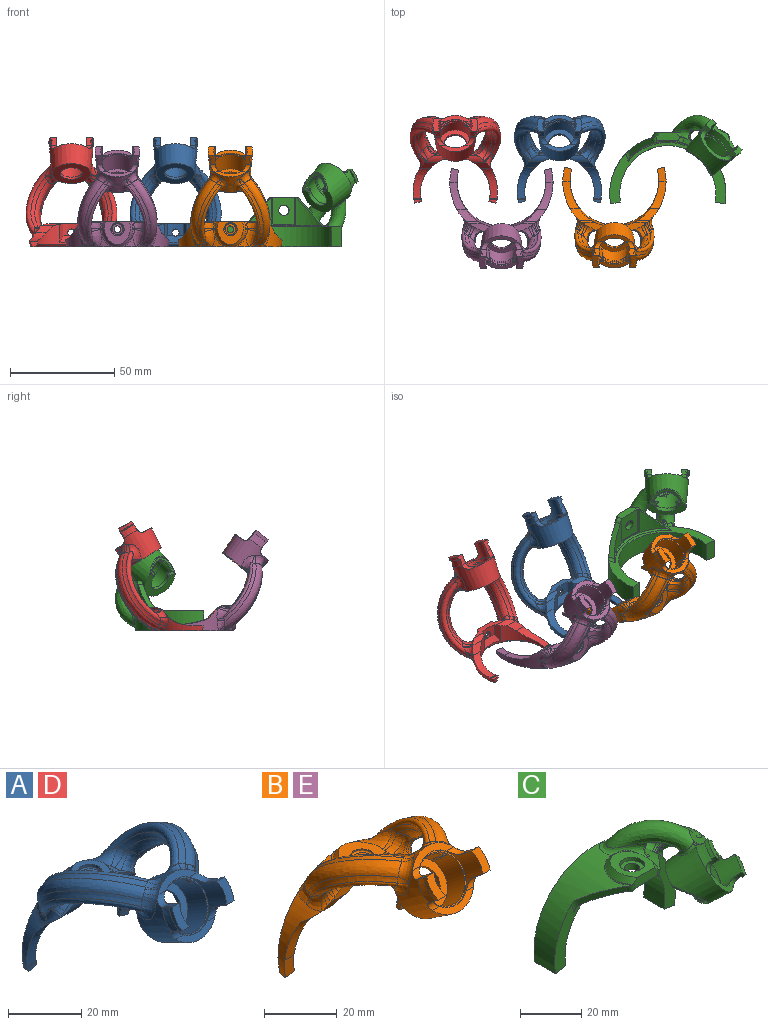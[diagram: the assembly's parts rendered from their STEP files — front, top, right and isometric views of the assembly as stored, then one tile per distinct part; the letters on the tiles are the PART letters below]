
ASSEMBLY  parts=5 mates=4
PART A: 145 faces, bbox 61.8x56.7x51.6 mm
  f0: cylinder r=1.71mm len=3.43mm, axis (0,0,-1), area 13.7mm2, adj f45,f46,f143
  f1: revolved ~9.98x7.31mm, area 15mm2, adj f23,f85,f86,f87,f132,f135
  f2: revolved ~9.98x7.51mm, area 16mm2, adj f23,f90,f92,f94,f130,f136
  f3: cone r=10.34mm half-angle=5deg, axis (0,-0.86,0.52), area 401.5mm2, adj f6,f7,f28,f50,f56,f57,f58,f59
  f4: revolved ~19.01x6.39mm, area 63.4mm2, adj f20,f23,f39,f40,f74,f75,f77
  f5: cone r=10.34mm half-angle=5deg, axis (0,-0.86,0.52), area 51.2mm2, adj f28,f53,f106,f108,f110,f116,f118,f120
  f6: cone r=10.34mm half-angle=8.4deg, axis (0,0.86,-0.52), area 23.4mm2, adj f3,f15,f51,f54,f58,f59
  f7: cone r=10.34mm half-angle=8.4deg, axis (0,0.86,-0.52), area 23.4mm2, adj f3,f16,f52,f55,f56,f57
  f8: plane 6.17x3.73mm, normal (0,0.86,-0.52), area 2.5mm2, adj f15,f18,f51,f54
  f9: plane 6.17x3.73mm, normal (0,0.86,-0.52), area 2.5mm2, adj f16,f17,f52,f55
  f10: cylinder r=10.72mm len=6.86mm, axis (0,0.86,-0.52), area 9.8mm2, adj f12,f18,f51,f54
  f11: cylinder r=10.72mm len=6.86mm, axis (0,0.86,-0.52), area 9.8mm2, adj f13,f17,f52,f55
  f12: plane 6.17x3.73mm, normal (0,-0.86,0.52), area 19.8mm2, adj f10,f14,f51,f54
  f13: plane 6.17x3.73mm, normal (0,-0.86,0.52), area 19.8mm2, adj f11,f14,f52,f55
  f14: cylinder r=8.05mm len=18.05mm, axis (0,0.86,-0.52), area 155.6mm2, adj f12,f13,f29,f50,f51,f52,f53,f54
  f15: cone r=9.87mm half-angle=40.8deg, axis (0,-0.86,0.52), area 2.8mm2, adj f6,f8,f51,f54
  f16: cone r=9.87mm half-angle=40.8deg, axis (0,-0.86,0.52), area 2.8mm2, adj f7,f9,f52,f55
  f17: cone r=10.46mm half-angle=45deg, axis (0,-0.86,0.52), area 2.6mm2, adj f9,f11,f52,f55
  f18: cone r=10.46mm half-angle=45deg, axis (0,-0.86,0.52), area 2.6mm2, adj f8,f10,f51,f54
  f19: plane 3.35x2.31mm, normal (-0.26,0,-0.97), area 6.5mm2, adj f21,f22,f23,f44,f49
  f20: plane 3.35x2.31mm, normal (0.26,0,-0.97), area 6.5mm2, adj f4,f21,f23,f39,f49
  f21: cylinder r=16.68mm len=33.35mm, axis (0,-1,0), area 210.6mm2, adj f19,f20,f39,f40,f41,f42,f43,f44
  f22: revolved ~18.79x6.34mm, area 62.2mm2, adj f19,f23,f42,f44,f93,f95,f97
  f23: plane 39.71x25.22mm, normal (0,1,0), area 110.1mm2, adj f1,f2,f4,f19,f20,f22,f49,f79
  f24: bspline ~37.35x28.39mm, area 142.5mm2, adj f72,f73,f74,f76,f78,f80,f123,f125
  f25: bspline ~37.42x27.73mm, area 153.3mm2, adj f70,f71,f83,f85,f120,f122
  f26: bspline ~41.55x31.99mm, area 181.1mm2, adj f71,f72,f77,f79,f115,f116,f117,f119
  f27: bspline ~33.51x27.06mm, area 100.4mm2, adj f70,f73,f84,f86,f126
  f28: plane 18.73x16.07mm, normal (0,0.86,-0.52), area 177.7mm2, adj f3,f5,f32,f109,f111,f112,f113,f114
  f29: plane 16.1x13.78mm, normal (0,-0.86,0.52), area 18.8mm2, adj f14,f30
  f30: cylinder r=7.67mm len=17.65mm, axis (0,0.86,-0.52), area 409.3mm2, adj f29,f31,f33,f60,f61,f62,f63,f64
  f31: plane 15.34x13.13mm, normal (0,-0.86,0.52), area 97mm2, adj f30,f32
  f32: cylinder r=5.29mm len=10.58mm, axis (0,0.86,-0.52), area 39.6mm2, adj f28,f31
  f33: bspline ~2.64x2.2mm, area 0.4mm2, adj f30,f34,f62,f64
  f34: plane 2.43x2.08mm, normal (0.71,-0.33,-0.62), area 1.2mm2, adj f33,f64
  f35: bspline ~37.68x29.01mm, area 144.5mm2, adj f68,f69,f97,f99,f100,f101,f107,f109
  f36: bspline ~41.92x32.7mm, area 183.6mm2, adj f67,f68,f91,f93,f102,f103,f104,f106
  f37: bspline ~37.76x28.35mm, area 155.8mm2, adj f66,f67,f88,f90,f110,f112
  f38: bspline ~33.81x27.63mm, area 102.1mm2, adj f66,f69,f94,f96,f113
  f39: plane 3.8x2.15mm, normal (0,-1,-0.01), area 6mm2, adj f4,f20,f21,f40
  f40: extruded ~15.06x8.21mm, area 65.8mm2, adj f4,f21,f39,f41,f76
  f41: plane 9.07x3.65mm, normal (0,-0.65,-0.76), area 23.4mm2, adj f21,f40,f78,f141
  f42: extruded ~15.06x8.21mm, area 65.7mm2, adj f21,f22,f43,f44,f99
  f43: plane 9.02x3.6mm, normal (0,-0.65,-0.76), area 23.4mm2, adj f21,f42,f101,f140
  f44: plane 3.8x2.15mm, normal (0,-1,-0.01), area 6mm2, adj f19,f21,f22,f42
  f45: cylinder r=18.71mm len=8.04mm, axis (0,1,0), area 37.7mm2, adj f0,f46,f47,f48,f139
  f46: cone r=18.71mm half-angle=34.2deg, axis (0,-1,0), area 35mm2, adj f0,f21,f45,f47,f48
  f47: plane 8.92x2.67mm, normal (-0.87,0,-0.5), area 20.9mm2, adj f21,f45,f46,f139,f140
  f48: plane 8.92x2.67mm, normal (0.87,0,-0.5), area 20.9mm2, adj f21,f45,f46,f139,f141
  f49: cone r=17.95mm half-angle=45deg, axis (0,1,0), area 114mm2, adj f19,f20,f21,f23
  f50: plane 15.23x2.96mm, normal (0,-0.86,0.52), area 27.9mm2, adj f3,f14,f57,f58
  f51: plane 3.92x2.9mm, normal (0,-0.52,-0.86), area 11.1mm2, adj f6,f8,f10,f12,f14,f15,f18,f58
  f52: plane 3.92x2.9mm, normal (0,-0.52,-0.86), area 11.1mm2, adj f7,f9,f11,f13,f14,f16,f17,f57
  f53: plane 15.28x3.01mm, normal (0,-0.86,0.52), area 27.9mm2, adj f5,f14,f56,f59,f104,f115
  f54: plane 3.92x2.9mm, normal (0,0.52,0.86), area 11.1mm2, adj f6,f8,f10,f12,f14,f15,f18,f59
  f55: plane 3.92x2.9mm, normal (0,0.52,0.86), area 11.1mm2, adj f7,f9,f11,f13,f14,f16,f17,f56
  f56: cylinder r=3.05mm len=5.14mm, axis (1,0,0), area 11.9mm2, adj f3,f7,f14,f53,f55,f117
  f57: cylinder r=3.05mm len=5.14mm, axis (-1,0,0), area 12.3mm2, adj f3,f7,f14,f50,f52
  f58: cylinder r=3.05mm len=5.14mm, axis (-1,0,0), area 12.3mm2, adj f3,f6,f14,f50,f51
  f59: cylinder r=3.05mm len=5.14mm, axis (1,0,0), area 11.9mm2, adj f3,f6,f14,f53,f54,f102
  f60: plane 0.56x0.38mm, normal (0.5,-0.45,-0.74), area 0.2mm2, adj f30,f62
  f61: plane 0.59x0.48mm, normal (1,0,0), area 0.2mm2, adj f30,f62
  f62: torus R=7.67mm, axis (0,0.86,-0.52), area 14.1mm2, adj f30,f33,f60,f61
  f63: plane 3.47x3.23mm, normal (0,0.86,-0.52), area 0.7mm2, adj f30,f65
  f64: plane 2.52x2.17mm, normal (0,0.86,-0.52), area 1.3mm2, adj f30,f33,f34
  f65: bspline ~3.11x2.87mm, area 0mm2, adj f30,f63
  f66: bspline ~26.78x13.96mm, area 61.4mm2, adj f37,f38,f92,f114
  f67: bspline ~36.44x19.97mm, area 96.7mm2, adj f36,f37,f89,f108
  f68: bspline ~35.96x20.27mm, area 92.1mm2, adj f35,f36,f95,f105
  f69: bspline ~25.43x11.92mm, area 58.4mm2, adj f35,f38,f98,f111
  f70: bspline ~26.88x14.18mm, area 60.2mm2, adj f25,f27,f87,f124
  f71: bspline ~36.63x19.85mm, area 95.2mm2, adj f25,f26,f81,f118
  f72: bspline ~36.32x20.23mm, area 91mm2, adj f24,f26,f75,f121
  f73: bspline ~26.06x11.92mm, area 57.5mm2, adj f24,f27,f82,f127
  f74: bspline ~4.95x4.54mm, area 10.4mm2, adj f4,f24,f75,f76
  f75: bspline ~4.6x3.59mm, area 5.8mm2, adj f4,f72,f74,f77
  f76: bspline ~4.82x1.66mm, area 1.4mm2, adj f24,f40,f74,f78
  f77: bspline ~4.12x4.07mm, area 7mm2, adj f4,f26,f75,f79
  f78: bspline ~7.43x4.67mm, area 15.9mm2, adj f24,f41,f76,f80
  f79: bspline ~4.9x4.45mm, area 8.3mm2, adj f23,f26,f77,f81
  f80: bspline ~5.35x4.42mm, area 4mm2, adj f24,f78,f82,f135
  f81: bspline ~2.23x2.21mm, area 3.1mm2, adj f23,f71,f79,f83
  f82: bspline ~5.38x4.83mm, area 8.9mm2, adj f73,f80,f84,f135
  f83: bspline ~4.27x3.14mm, area 5.5mm2, adj f23,f25,f81,f85
  f84: bspline ~7.41x6.36mm, area 19.1mm2, adj f27,f82,f86,f135
  f85: bspline ~8.52x5.93mm, area 28.3mm2, adj f1,f25,f83,f87
  f86: bspline ~5.81x5.01mm, area 8.1mm2, adj f1,f27,f84,f87
  f87: bspline ~5.9x5.71mm, area 11.1mm2, adj f1,f70,f85,f86
  f88: bspline ~4.19x3.05mm, area 5.3mm2, adj f23,f37,f89,f90
  f89: bspline ~2.45x2.27mm, area 2.6mm2, adj f23,f67,f88,f91
  f90: bspline ~8.51x6.25mm, area 27.7mm2, adj f2,f37,f88,f92
  f91: bspline ~4.59x4.34mm, area 7.9mm2, adj f23,f36,f89,f93
  f92: bspline ~5.96x5.71mm, area 11mm2, adj f2,f66,f90,f94
  f93: bspline ~4.04x3.98mm, area 6.2mm2, adj f22,f36,f91,f95
  f94: bspline ~5.8x4.97mm, area 9.3mm2, adj f2,f38,f92,f96
  f95: bspline ~4.79x4.1mm, area 5.8mm2, adj f22,f68,f93,f97
  f96: bspline ~7.04x6.2mm, area 18.8mm2, adj f38,f94,f98,f136
  f97: bspline ~4.94x4.53mm, area 10.9mm2, adj f22,f35,f95,f99
  f98: bspline ~5.01x4.29mm, area 9.3mm2, adj f69,f96,f100,f136
  f99: bspline ~5.07x1.75mm, area 1.7mm2, adj f35,f42,f97,f101
  f100: bspline ~5.51x4.35mm, area 3.8mm2, adj f35,f98,f101,f136
  f101: bspline ~7.24x4.5mm, area 16.3mm2, adj f35,f43,f99,f100
  f102: bspline ~4.68x2.61mm, area 4.9mm2, adj f36,f59,f103,f104
  f103: bspline ~4.3x2.78mm, area 4.5mm2, adj f3,f36,f102,f105
  f104: bspline ~4.31x3.58mm, area 7.9mm2, adj f36,f53,f102,f106
  f105: bspline ~4.28x3.35mm, area 6.7mm2, adj f3,f68,f103,f107
  f106: bspline ~4.48x4.06mm, area 2.6mm2, adj f5,f36,f104,f108
  f107: bspline ~8.07x7.07mm, area 32.8mm2, adj f3,f35,f105,f109
  f108: bspline ~5.63x4.91mm, area 6.6mm2, adj f5,f67,f106,f110
  f109: bspline ~4.59x3.99mm, area 3mm2, adj f28,f35,f107,f111
  f110: bspline ~8.42x5.7mm, area 32.1mm2, adj f5,f37,f108,f112
  f111: bspline ~4.41x4.21mm, area 7.9mm2, adj f28,f69,f109,f113
  f112: bspline ~4.59x4.07mm, area 3.3mm2, adj f28,f37,f110,f114
  f113: bspline ~6.86x6.15mm, area 19.8mm2, adj f28,f38,f111,f114
  f114: bspline ~4.88x4.18mm, area 7.7mm2, adj f28,f66,f112,f113
  f115: bspline ~4.3x3.41mm, area 7.4mm2, adj f26,f53,f116,f117
  f116: bspline ~4.74x4.27mm, area 3.2mm2, adj f5,f26,f115,f118
  f117: bspline ~4.79x2.54mm, area 4.6mm2, adj f26,f56,f115,f119
  f118: bspline ~5.48x4.68mm, area 6.5mm2, adj f5,f71,f116,f120
  f119: bspline ~4.37x3.28mm, area 4.9mm2, adj f3,f26,f117,f121
  f120: bspline ~8.77x5.83mm, area 31.6mm2, adj f5,f25,f118,f122
  f121: bspline ~4.23x3.71mm, area 6.6mm2, adj f3,f72,f119,f123
  f122: bspline ~4.69x4.02mm, area 3.6mm2, adj f25,f28,f120,f124
  f123: bspline ~8.17x7.09mm, area 32.4mm2, adj f3,f24,f121,f125
  f124: bspline ~4.87x4.1mm, area 7.6mm2, adj f28,f70,f122,f126
  f125: bspline ~4.58x3.99mm, area 3.3mm2, adj f24,f28,f123,f127
  f126: bspline ~6.85x6.08mm, area 19.6mm2, adj f27,f28,f124,f127
  f127: bspline ~4.34x4.21mm, area 7.8mm2, adj f28,f73,f125,f126
  f128: plane 10.44x9.55mm, normal (0,0,1), area 49mm2, adj f129,f133,f138,f139,f142
  f129: bspline ~12.16x10.1mm, area 37.9mm2, adj f128,f130,f131,f132,f133,f138
  f130: bspline ~10.56x6.01mm, area 9.4mm2, adj f2,f129,f131,f137
  f131: bspline ~3.34x0.73mm, area 1.8mm2, adj f23,f129,f130,f132
  f132: bspline ~10.55x6.11mm, area 9.5mm2, adj f1,f129,f131,f134
  f133: extruded ~1.27x1.03mm, area 1.7mm2, adj f128,f129,f134,f139
  f134: extruded ~1.02x0.69mm, area 0.9mm2, adj f132,f133,f135,f139
  f135: cylinder r=20.42mm len=8.45mm, axis (0,1,0), area 7.6mm2, adj f1,f80,f82,f84,f134,f139,f141
  f136: cylinder r=20.42mm len=8.45mm, axis (0,1,0), area 7.6mm2, adj f2,f96,f98,f100,f137,f139,f140
  f137: extruded ~1.02x0.69mm, area 0.9mm2, adj f130,f136,f138,f139
  f138: extruded ~1.27x1.04mm, area 1.7mm2, adj f128,f129,f137,f139
  f139: plane 21.33x3.84mm, normal (0,-1,0), area 43.9mm2, adj f45,f47,f48,f128,f133,f134,f135,f136
  f140: cylinder r=5.08mm len=10mm, axis (-1,0,0), area 21.7mm2, adj f21,f43,f47,f136,f139
  f141: cylinder r=5.08mm len=10mm, axis (-1,0,0), area 21.7mm2, adj f21,f41,f48,f135,f139
  f142: cylinder r=3.17mm len=6.35mm, axis (0,0,1), area 17.7mm2, adj f128,f144
  f143: plane 5.59x5.59mm, normal (0,0,1), area 15.3mm2, adj f0,f144
  f144: torus R=2.79mm, axis (0,0,1), area 11.4mm2, adj f142,f143
PART B: 144 faces, bbox 51.7x52.7x52.5 mm
  f0: revolved ~5.9x5.45mm, area 16.2mm2, adj f1,f142,f143
  f1: bspline ~9.37x6.34mm, area 36.9mm2, adj f0,f2,f139,f140,f141
  f2: bspline ~3.52x1.42mm, area 2.6mm2, adj f1,f3,f138,f142
  f3: bspline ~1.16x0.78mm, area 0.5mm2, adj f2,f4,f138,f139
  f4: bspline ~2.44x0.93mm, area 1mm2, adj f3,f5,f137,f138
  f5: bspline ~4.62x2.02mm, area 1.5mm2, adj f4,f6,f136,f138
  f6: plane 31.53x6.21mm, normal (0,-1,0), area 81.9mm2, adj f5,f7,f115,f116,f117,f118,f119,f120
  f7: bspline ~7.06x6.66mm, area 17.5mm2, adj f6,f8,f115,f137
  f8: bspline ~31.43x23.43mm, area 79.9mm2, adj f7,f9,f113,f114,f115,f137
  f9: bspline ~7.85x6mm, area 21.3mm2, adj f8,f10,f111,f112
  f10: bspline ~4.41x4.15mm, area 5.6mm2, adj f9,f11,f111,f113
  f11: bspline ~4.68x3.98mm, area 3.4mm2, adj f10,f12,f110,f111
  f12: bspline ~7.34x7.29mm, area 24.7mm2, adj f11,f13,f77,f110
  f13: bspline ~3.66x3.46mm, area 4.1mm2, adj f12,f14,f76,f77
  f14: bspline ~29.57x16.47mm, area 58.5mm2, adj f13,f15,f75,f110
  f15: bspline ~37.48x26.76mm, area 197.7mm2, adj f14,f16,f18,f71,f76
  f16: bspline ~4.26x4mm, area 8.3mm2, adj f15,f17,f18,f143
  f17: bspline ~2.32x1.83mm, area 2.2mm2, adj f16,f71,f141,f143
  f18: bspline ~6.58x3.99mm, area 14.2mm2, adj f15,f16,f19,f75
  f19: revolved ~25.27x10.85mm, area 119.7mm2, adj f18,f20,f65,f66,f67,f70,f75,f143
  f20: plane 3.32x2.46mm, normal (-0.26,0,-0.97), area 7.2mm2, adj f19,f21,f61,f65,f143
  f21: cone r=22.48mm half-angle=45deg, axis (0,1,0), area 143.8mm2, adj f20,f22,f61,f143
  f22: plane 3.32x2.46mm, normal (0.26,0,-0.97), area 7.2mm2, adj f21,f23,f60,f61,f143
  f23: revolved ~25.27x10.85mm, area 119.7mm2, adj f22,f24,f25,f57,f58,f59,f60,f143
  f24: extruded ~13.06x7.87mm, area 47.1mm2, adj f23,f59,f60,f61,f127
  f25: bspline ~6.36x3.99mm, area 14.2mm2, adj f23,f26,f56,f57
  f26: bspline ~37.36x26.53mm, area 197.7mm2, adj f25,f27,f54,f55,f56
  f27: bspline ~30.31x17.11mm, area 63mm2, adj f26,f28,f52,f53
  f28: bspline ~32.11x22.21mm, area 73.8mm2, adj f27,f29,f30,f49,f50,f51
  f29: bspline ~3.34x2.6mm, area 5.3mm2, adj f28,f30,f52,f143
  f30: bspline ~9.45x6.34mm, area 36.9mm2, adj f28,f29,f31,f46,f48
  f31: bspline ~5.88x5.41mm, area 8.6mm2, adj f30,f32,f45,f49
  f32: bspline ~7.73x7.32mm, area 19.3mm2, adj f31,f33,f34,f132,f133
  f33: bspline ~2.1x0.93mm, area 1mm2, adj f32,f45,f134,f138
  f34: bspline ~31.34x23.25mm, area 79.9mm2, adj f32,f35,f44,f49,f131,f132
  f35: bspline ~7.65x5.73mm, area 21.3mm2, adj f34,f36,f37,f111
  f36: bspline ~4.62x3.32mm, area 5.4mm2, adj f35,f49,f50,f111
  f37: bspline ~4.07x3.8mm, area 5.6mm2, adj f35,f38,f44,f111
  f38: bspline ~4.68x3.98mm, area 3.4mm2, adj f37,f39,f41,f111
  f39: bspline ~7.28x7.11mm, area 24.7mm2, adj f38,f40,f41,f77
  f40: bspline ~3.67x3.46mm, area 4.1mm2, adj f39,f54,f55,f77
  f41: bspline ~31.99x22.24mm, area 63.3mm2, adj f38,f39,f42,f43,f44,f55,f58,f129
  f42: bspline ~6.43x3.18mm, area 5.9mm2, adj f41,f43,f128,f129
  f43: bspline ~6.48x2.48mm, area 7.3mm2, adj f41,f42,f58,f59
  f44: bspline ~18.17x8.9mm, area 29.3mm2, adj f34,f37,f41,f130
  f45: bspline ~1.29x0.79mm, area 0.5mm2, adj f31,f33,f46,f138
  f46: bspline ~3.42x1.38mm, area 2.6mm2, adj f30,f45,f47,f138
  f47: bspline ~8.27x7.02mm, area 6.9mm2, adj f46,f48,f138,f143
  f48: revolved ~5.9x5.43mm, area 16.2mm2, adj f30,f47,f143
  f49: bspline ~19.92x10.54mm, area 33.9mm2, adj f28,f31,f34,f36
  f50: bspline ~5.03x3.37mm, area 3.5mm2, adj f28,f36,f51,f111
  f51: bspline ~7.67x5.95mm, area 25.3mm2, adj f28,f50,f53,f77
  f52: bspline ~2.22x1.83mm, area 2.2mm2, adj f27,f29,f56,f143
  f53: bspline ~4.08x3.49mm, area 3.9mm2, adj f27,f51,f54,f77
  f54: bspline ~6.37x5.96mm, area 25.9mm2, adj f26,f40,f53,f77
  f55: bspline ~30.38x17.67mm, area 58.5mm2, adj f26,f40,f41,f57
  f56: bspline ~4.26x4mm, area 8.3mm2, adj f25,f26,f52,f143
  f57: bspline ~4x2.79mm, area 3.8mm2, adj f23,f25,f55,f58
  f58: bspline ~6.77x5.55mm, area 18.5mm2, adj f23,f41,f43,f57
  f59: extruded ~10.01x5.6mm, area 39.4mm2, adj f23,f24,f43,f127,f128
  f60: plane 6.61x4.24mm, normal (0,-1,-0.09), area 21.7mm2, adj f22,f23,f24,f61
  f61: cylinder r=21.21mm len=42.42mm, axis (0,-1,0), area 188.4mm2, adj f20,f21,f22,f24,f60,f62,f65,f66
  f62: cone r=21.21mm half-angle=49.7deg, axis (0,-1,0), area 33.6mm2, adj f61,f63,f64,f120,f121,f126
  f63: plane 5.59x0.59mm, normal (0.98,0,0.2), area 1.5mm2, adj f62,f121,f126
  f64: plane 5.59x0.59mm, normal (-0.98,0,0.2), area 1.5mm2, adj f62,f120,f121
  f65: plane 6.61x4.24mm, normal (0,-1,-0.09), area 21.7mm2, adj f19,f20,f61,f66
  f66: extruded ~13.06x7.87mm, area 47.1mm2, adj f19,f61,f65,f67,f119
  f67: extruded ~10.01x5.6mm, area 39.4mm2, adj f19,f66,f68,f118,f119
  f68: bspline ~6.42x2.52mm, area 7.3mm2, adj f67,f69,f70,f110
  f69: bspline ~5.63x2.66mm, area 5.9mm2, adj f68,f110,f117,f118
  f70: bspline ~7.41x5.93mm, area 18.5mm2, adj f19,f68,f75,f110
  f71: bspline ~30.59x17.18mm, area 63mm2, adj f15,f17,f72,f140
  f72: bspline ~4.14x3.53mm, area 3.9mm2, adj f71,f73,f76,f77
  f73: bspline ~7.3x5.58mm, area 25.3mm2, adj f72,f74,f77,f140
  f74: bspline ~5.03x3.37mm, area 3.5mm2, adj f73,f111,f112,f140
  f75: bspline ~4.01x2.74mm, area 3.8mm2, adj f14,f18,f19,f70
  f76: bspline ~6.37x5.96mm, area 25.9mm2, adj f13,f15,f72,f77
  f77: cone r=10.34mm half-angle=5deg, axis (0,-0.78,0.62), area 474.5mm2, adj f12,f13,f39,f40,f51,f53,f54,f72
  f78: cylinder r=2.54mm len=4.48mm, axis (-1,0,0), area 10.6mm2, adj f77,f79,f99,f109
  f79: cylinder r=8.05mm len=17.74mm, axis (0,0.78,-0.62), area 152.6mm2, adj f78,f80,f83,f86,f99,f101,f102,f103
  f80: plane 5.64x4.49mm, normal (0,-0.78,0.62), area 19.8mm2, adj f79,f81,f105,f107
  f81: cylinder r=10.72mm len=6.63mm, axis (0,0.78,-0.62), area 11.7mm2, adj f80,f82,f105,f107
  f82: plane 5.64x4.49mm, normal (0,0.78,-0.62), area 6.6mm2, adj f81,f105,f106,f107
  f83: plane 5.64x4.49mm, normal (0,-0.78,0.62), area 19.8mm2, adj f79,f84,f99,f101
  f84: cylinder r=10.72mm len=6.63mm, axis (0,0.78,-0.62), area 11.7mm2, adj f83,f85,f99,f101
  f85: plane 5.64x4.49mm, normal (0,0.78,-0.62), area 6.6mm2, adj f84,f99,f100,f101
  f86: plane 16.1x12.6mm, normal (0,-0.78,0.62), area 18.8mm2, adj f79,f87
  f87: cylinder r=7.67mm len=17.44mm, axis (0,0.78,-0.62), area 404.9mm2, adj f86,f88,f89,f90,f91,f93,f94,f95
  f88: plane 0.33x0.31mm, normal (0,-0.78,0.62), area 0mm2, adj f87,f90,f98
  f89: bspline ~0.57x0.55mm, area 0mm2, adj f87,f90
  f90: plane 4.86x4.16mm, normal (-0.77,-0.4,-0.5), area 3.7mm2, adj f87,f88,f89,f97,f98
  f91: plane 15.34x12mm, normal (0,-0.78,0.62), area 97mm2, adj f87,f92
  f92: cylinder r=5.29mm len=10.58mm, axis (0,0.78,-0.62), area 39.6mm2, adj f91,f111
  f93: bspline ~0.57x0.55mm, area 0mm2, adj f87,f94
  f94: plane 4.86x4.16mm, normal (0.77,-0.4,-0.5), area 3.7mm2, adj f87,f93,f95,f96,f97
  f95: plane 0.33x0.31mm, normal (0,-0.78,0.62), area 0mm2, adj f87,f94,f96
  f96: plane 2.73x2.18mm, normal (0,-0.62,-0.78), area 0.3mm2, adj f87,f94,f95,f97
  f97: torus R=7.67mm, axis (0,0.78,-0.62), area 12.5mm2, adj f87,f90,f94,f96,f98
  f98: plane 2.73x2.18mm, normal (0,-0.62,-0.78), area 0.3mm2, adj f87,f88,f90,f97
  f99: plane 3.98x3.17mm, normal (0,-0.62,-0.78), area 12.4mm2, adj f77,f78,f79,f83,f84,f85,f100
  f100: cone r=10.34mm half-angle=8.4deg, axis (0,0.78,-0.62), area 25.6mm2, adj f77,f85,f99,f101
  f101: plane 3.98x3.17mm, normal (0,0.62,0.78), area 12.4mm2, adj f77,f79,f83,f84,f85,f100,f102
  f102: cylinder r=2.54mm len=4.48mm, axis (1,0,0), area 10.6mm2, adj f77,f79,f101,f103
  f103: plane 16.06x3.1mm, normal (0,-0.78,0.62), area 30.9mm2, adj f77,f79,f102,f104
  f104: cylinder r=2.54mm len=4.48mm, axis (1,0,0), area 10.6mm2, adj f77,f79,f103,f105
  f105: plane 3.98x3.17mm, normal (0,0.62,0.78), area 12.4mm2, adj f77,f79,f80,f81,f82,f104,f106
  f106: cone r=10.34mm half-angle=8.4deg, axis (0,0.78,-0.62), area 25.6mm2, adj f77,f82,f105,f107
  f107: plane 3.98x3.17mm, normal (0,-0.62,-0.78), area 12.4mm2, adj f77,f79,f80,f81,f82,f106,f108
  f108: cylinder r=2.54mm len=4.48mm, axis (-1,0,0), area 10.6mm2, adj f77,f79,f107,f109
  f109: plane 16.06x3.1mm, normal (0,-0.78,0.62), area 30.9mm2, adj f77,f78,f79,f108
  f110: bspline ~32.08x22.44mm, area 63.3mm2, adj f11,f12,f14,f68,f69,f70,f113,f117
  f111: plane 19.43x15.42mm, normal (0,0.78,-0.62), area 177.7mm2, adj f9,f10,f11,f35,f36,f37,f38,f50
  f112: bspline ~4.65x3.41mm, area 5.4mm2, adj f9,f74,f111,f114
  f113: bspline ~17.97x8.7mm, area 29.3mm2, adj f8,f10,f110,f116
  f114: bspline ~20.19x10.81mm, area 33.9mm2, adj f8,f112,f139,f140
  f115: bspline ~5.61x3.54mm, area 6.6mm2, adj f6,f7,f8,f116
  f116: bspline ~5.18x4.31mm, area 6.8mm2, adj f6,f113,f115,f117
  f117: bspline ~6.01x3.84mm, area 5.7mm2, adj f6,f69,f110,f116
  f118: plane 7.18x0.97mm, normal (0,-0.91,-0.41), area 5.9mm2, adj f6,f67,f69,f119
  f119: cone r=21.21mm half-angle=6.1deg, axis (0,-1,0), area 91.8mm2, adj f6,f61,f66,f67,f118,f120
  f120: bspline ~8.94x2.98mm, area 17.3mm2, adj f6,f62,f64,f119,f121
  f121: cylinder r=23.7mm len=9.6mm, axis (0,-1,0), area 47.7mm2, adj f6,f62,f63,f64,f120,f122,f126
  f122: cylinder r=1.59mm len=3.18mm, axis (0,0,-1), area 16.2mm2, adj f121,f123
  f123: revolved ~5.26x5.23mm, area 13.7mm2, adj f122,f124
  f124: bspline ~6.36x6.36mm, area 15.8mm2, adj f123,f125
  f125: cylinder r=3.17mm len=6.35mm, axis (0,0,-1), area 4.9mm2, adj f124,f135
  f126: bspline ~8.94x2.98mm, area 17.3mm2, adj f6,f62,f63,f121,f127
  f127: cone r=21.21mm half-angle=6.1deg, axis (0,-1,0), area 91.8mm2, adj f6,f24,f59,f61,f126,f128
  f128: plane 7.18x0.97mm, normal (0,-0.91,-0.41), area 5.9mm2, adj f6,f42,f59,f127
  f129: bspline ~6.32x4.03mm, area 5.7mm2, adj f6,f41,f42,f130
  f130: bspline ~4.97x3.29mm, area 6.8mm2, adj f6,f44,f129,f131
  f131: bspline ~5.73x3.57mm, area 6.6mm2, adj f6,f34,f130,f132
  f132: bspline ~7.06x6.66mm, area 17.5mm2, adj f6,f32,f34,f131
  f133: revolved ~1.76x0.63mm, area 0.6mm2, adj f6,f32,f134
  f134: bspline ~3.97x1.74mm, area 1.5mm2, adj f6,f33,f133,f138
  f135: plane 12.69x10.98mm, normal (0,0,1), area 81.1mm2, adj f6,f125,f138
  f136: revolved ~1.76x0.63mm, area 0.6mm2, adj f5,f6,f137
  f137: bspline ~7.38x7.09mm, area 19.3mm2, adj f4,f7,f8,f136,f139
  f138: bspline ~14.7x12.5mm, area 54.1mm2, adj f2,f3,f4,f5,f6,f33,f45,f46
  f139: bspline ~5.9x5.43mm, area 8.6mm2, adj f1,f3,f114,f137
  f140: bspline ~32.21x22.41mm, area 73.8mm2, adj f1,f71,f73,f74,f114,f141
  f141: bspline ~3.34x2.6mm, area 5.3mm2, adj f1,f17,f140,f143
  f142: bspline ~8.15x6.79mm, area 6.9mm2, adj f0,f2,f138,f143
  f143: plane 49.22x31.49mm, normal (0,1,0), area 164.7mm2, adj f0,f16,f17,f19,f20,f21,f22,f23
PART C: 97 faces, bbox 66.4x42.7x43 mm
  f0: bspline ~3.37x2.3mm, area 3mm2, adj f1,f11,f61,f81
  f1: bspline ~3.97x1.98mm, area 2.3mm2, adj f0,f2,f11,f61
  f2: bspline ~4.2x2.14mm, area 3.4mm2, adj f1,f6,f11,f82
  f3: cylinder r=2.48mm len=4.95mm, axis (0,0,-1), area 37.8mm2, adj f23,f72
  f4: cylinder r=2.54mm len=3.25mm, axis (-0.28,0,0.96), area 7.4mm2, adj f7,f24,f30,f62,f70,f72,f74,f76
  f5: cylinder r=2.54mm len=3.25mm, axis (-0.28,0,-0.96), area 7.4mm2, adj f6,f24,f30,f61,f70,f72,f75,f78
  f6: cylinder r=27.82mm len=31.94mm, axis (0,-1,0), area 313.2mm2, adj f2,f5,f8,f9,f25,f27,f28,f61
  f7: cylinder r=27.82mm len=32.65mm, axis (0,-1,0), area 548.9mm2, adj f4,f9,f25,f27,f29,f62,f67,f76
  f8: bspline ~5.14x2.62mm, area 3.9mm2, adj f6,f9,f22,f63
  f9: bspline ~15.52x11.85mm, area 51.7mm2, adj f6,f7,f8,f22,f64,f77
  f10: cone r=10.34mm half-angle=4.9deg, axis (0.59,-0.54,0.59), area 628.2mm2, adj f13,f14,f34,f43,f46,f47,f49,f50
  f11: bspline ~33.94x22.52mm, area 259.8mm2, adj f0,f1,f2,f43,f79,f80,f81,f82
  f12: cone r=10.34mm half-angle=4.9deg, axis (0.59,-0.54,0.59), area 0mm2, adj f43,f52,f94
  f13: cone r=10.34mm half-angle=8.1deg, axis (-0.59,0.54,-0.59), area 28.8mm2, adj f10,f16,f42,f45,f47,f48,f51,f96
  f14: cone r=10.34mm half-angle=8.1deg, axis (-0.59,0.54,-0.59), area 29mm2, adj f10,f15,f41,f44,f49,f50
  f15: plane 6.06x3.44mm, normal (-0.59,0.54,-0.59), area 6.6mm2, adj f14,f17,f41,f44
  f16: plane 6.06x3.44mm, normal (-0.59,0.54,-0.59), area 6.6mm2, adj f13,f18,f42,f45
  f17: cylinder r=10.72mm len=6.82mm, axis (-0.59,0.54,-0.59), area 10.3mm2, adj f15,f19,f41,f44
  f18: cylinder r=10.72mm len=6.82mm, axis (-0.59,0.54,-0.59), area 10.3mm2, adj f16,f20,f42,f45
  f19: plane 6.06x4.81mm, normal (0.59,-0.54,0.59), area 19.8mm2, adj f17,f21,f41,f44
  f20: plane 6.06x4.81mm, normal (0.59,-0.54,0.59), area 19.8mm2, adj f18,f21,f42,f45
  f21: cylinder r=8.05mm len=18.01mm, axis (-0.59,0.54,-0.59), area 253.1mm2, adj f19,f20,f35,f41,f42,f43,f44,f45
  f22: bspline ~25.46x22.2mm, area 518mm2, adj f8,f9,f43,f48,f51,f52,f63,f64
  f23: cylinder r=27.82mm len=8.1mm, axis (0,-1,0), area 32.4mm2, adj f3,f68
  f24: cylinder r=25.28mm len=35.55mm, axis (0,-1,0), area 190.9mm2, adj f4,f5,f61,f62,f65,f71,f73,f74
  f25: plane 56.4x30.11mm, normal (0,-1,0), area 282.6mm2, adj f6,f7,f26,f28,f29,f65,f66,f67
  f26: cylinder r=22.99mm len=45.98mm, axis (0,-1,0), area 764.4mm2, adj f25,f27,f28,f29
  f27: plane 55.68x32.69mm, normal (0,1,0), area 428mm2, adj f6,f7,f26,f28,f29,f64
  f28: plane 9.53x4.75mm, normal (-0.17,0,-0.98), area 46mm2, adj f6,f25,f26,f27
  f29: plane 9.53x4.75mm, normal (0.17,0,-0.98), area 46mm2, adj f7,f25,f26,f27
  f30: plane 11.35x3.85mm, normal (0,-1,0), area 39mm2, adj f4,f5,f69,f70,f72
  f31: bspline ~29.27x17.08mm, area 66.5mm2, adj f79,f80,f87,f92,f93,f94
  f32: cylinder r=7.67mm len=17.45mm, axis (-0.59,0.54,-0.59), area 348.9mm2, adj f35,f36,f38,f39,f40,f53,f54,f56
  f33: cylinder r=5.29mm len=9.57mm, axis (-0.59,0.54,-0.59), area 38.3mm2, adj f34,f36,f53,f55,f56,f58
  f34: plane 14.78x14.78mm, normal (-0.59,0.54,-0.59), area 111.2mm2, adj f10,f33,f55,f57,f58,f59,f60
  f35: plane 13.53x12.95mm, normal (0.59,-0.54,0.59), area 18.8mm2, adj f21,f32
  f36: plane 12.34x12.34mm, normal (0.59,-0.54,0.59), area 65.4mm2, adj f32,f33,f53,f56
  f37: cylinder r=22.23mm len=11.01mm, axis (0,1,0), area 25.7mm2, adj f53,f54,f55,f56,f57,f58,f59,f60
  f38: torus R=7.67mm, axis (-0.59,0.54,-0.59), area 23.4mm2, adj f32,f39,f40
  f39: plane 0.49x0.41mm, normal (0.71,0,-0.71), area 0.2mm2, adj f32,f38
  f40: plane 0.49x0.41mm, normal (0.71,0,-0.71), area 0.2mm2, adj f32,f38
  f41: plane 3.56x3.01mm, normal (0.38,0.84,0.38), area 6.4mm2, adj f14,f15,f17,f19,f21,f50
  f42: plane 3.56x3.01mm, normal (0.38,0.84,0.38), area 6.4mm2, adj f13,f16,f18,f20,f21,f48
  f43: plane 14.59x12.96mm, normal (0.59,-0.54,0.59), area 53.7mm2, adj f10,f11,f12,f21,f22,f48,f50,f52
  f44: plane 3.56x3.01mm, normal (-0.38,-0.84,-0.38), area 6.4mm2, adj f14,f15,f17,f19,f21,f49
  f45: plane 3.56x3.01mm, normal (-0.38,-0.84,-0.38), area 6.4mm2, adj f13,f16,f18,f20,f21,f47
  f46: plane 11.74x11.74mm, normal (0.59,-0.54,0.59), area 35mm2, adj f10,f21,f47,f49
  f47: cylinder r=2.54mm len=5.4mm, axis (-0.71,0,0.71), area 9.5mm2, adj f10,f13,f21,f45,f46
  f48: cylinder r=2.54mm len=3.99mm, axis (0.71,0,-0.71), area 10.9mm2, adj f13,f21,f22,f42,f43,f96
  f49: cylinder r=2.54mm len=5.4mm, axis (-0.71,0,0.71), area 9.5mm2, adj f10,f14,f21,f44,f46
  f50: cylinder r=2.54mm len=3.73mm, axis (0.71,0,-0.71), area 9.5mm2, adj f10,f14,f21,f41,f43
  f51: bspline ~7.62x7.24mm, area 26.3mm2, adj f10,f13,f22,f90,f96
  f52: bspline ~1.89x1.85mm, area 0.8mm2, adj f12,f22,f43,f93
  f53: bspline ~2.96x2.15mm, area 3.1mm2, adj f32,f33,f36,f37,f54,f55
  f54: bspline ~10.37x10.35mm, area 17.1mm2, adj f32,f37,f53,f56
  f55: bspline ~3.79x1.85mm, area 1.6mm2, adj f33,f34,f37,f53,f57
  f56: bspline ~2.96x2.15mm, area 3.1mm2, adj f32,f33,f36,f37,f54,f58
  f57: bspline ~2.86x1.73mm, area 1mm2, adj f34,f37,f55,f59
  f58: bspline ~3.78x1.85mm, area 1.6mm2, adj f33,f34,f37,f56,f60
  f59: bspline ~12.78x12.71mm, area 15.5mm2, adj f10,f34,f37,f57,f60
  f60: bspline ~2.86x1.73mm, area 1mm2, adj f34,f37,f58,f59
  f61: plane 12.34x11.8mm, normal (0.68,-0.71,-0.2), area 44.5mm2, adj f0,f1,f5,f6,f24,f65,f66
  f62: plane 12.34x11.8mm, normal (-0.68,-0.71,-0.2), area 44.6mm2, adj f4,f7,f24,f65,f67
  f63: bspline ~14.59x9.57mm, area 62.7mm2, adj f6,f8,f22,f64
  f64: bspline ~5.34x2.4mm, area 9.7mm2, adj f9,f22,f27,f63
  f65: torus R=24.52mm, axis (0,-1,0), area 49.3mm2, adj f24,f25,f61,f62,f66,f67
  f66: cylinder r=2.54mm len=5.13mm, axis (0.28,0,0.96), area 6.7mm2, adj f25,f61,f65,f81
  f67: cylinder r=2.54mm len=5.13mm, axis (-0.28,0,0.96), area 6.7mm2, adj f7,f25,f62,f65
  f68: cylinder r=4.05mm len=8.1mm, axis (0,0,-1), area 39.9mm2, adj f23,f69
  f69: plane 14.56x12.49mm, normal (0,0,1), area 99mm2, adj f30,f68,f70
  f70: bspline ~16.85x15.93mm, area 82.6mm2, adj f4,f5,f30,f69,f76,f77,f78
  f71: plane 5.8x0.67mm, normal (0,-1,0), area 1.1mm2, adj f24,f72,f75
  f72: plane 12.98x10.54mm, normal (0,0,-1), area 117.5mm2, adj f3,f4,f5,f30,f71,f73,f74,f75
  f73: plane 5.8x0.67mm, normal (0,-1,0), area 1.1mm2, adj f24,f72,f74
  f74: plane 12.99x0.68mm, normal (0.78,0,-0.62), area 11.1mm2, adj f4,f24,f72,f73
  f75: plane 12.99x0.68mm, normal (-0.78,0,-0.62), area 11.1mm2, adj f5,f24,f71,f72
  f76: bspline ~16.94x9.39mm, area 7.2mm2, adj f4,f7,f70,f77
  f77: bspline ~8.35x7.43mm, area 8.1mm2, adj f9,f70,f76,f78
  f78: bspline ~10.46x2.71mm, area 3.1mm2, adj f5,f6,f70,f77
  f79: bspline ~15.24x7.09mm, area 35.4mm2, adj f11,f31,f85,f89,f90,f91
  f80: bspline ~22.01x10.36mm, area 61.1mm2, adj f11,f31,f43,f86,f95
  f81: bspline ~2.75x1.97mm, area 3.1mm2, adj f0,f11,f66,f83
  f82: bspline ~4.16x3.47mm, area 4mm2, adj f2,f6,f11,f85
  f83: bspline ~4.73x3.66mm, area 8.7mm2, adj f11,f25,f81,f84
  f84: bspline ~9.85x6.65mm, area 35.9mm2, adj f6,f11,f83,f86
  f85: bspline ~8.63x7.1mm, area 11.4mm2, adj f6,f79,f82,f87
  f86: bspline ~5.96x5.04mm, area 6.4mm2, adj f6,f80,f84,f87
  f87: bspline ~7.85x4.53mm, area 18.9mm2, adj f6,f31,f85,f86
  f88: bspline ~7.26x5.29mm, area 8.8mm2, adj f10,f11,f43,f89
  f89: bspline ~3.6x2.51mm, area 0.5mm2, adj f10,f79,f88,f90
  f90: bspline ~2.21x0.91mm, area 1.2mm2, adj f51,f79,f89,f91
  f91: bspline ~3.69x2.54mm, area 0.7mm2, adj f22,f79,f90,f92
  f92: bspline ~3.15x2.03mm, area 3.1mm2, adj f22,f31,f91,f93
  f93: bspline ~1.31x1.13mm, area 0.7mm2, adj f31,f52,f92,f94
  f94: bspline ~1.19x0.78mm, area 0.1mm2, adj f12,f31,f43,f93,f95
  f95: bspline ~3.92x2mm, area 0.6mm2, adj f43,f80,f94
  f96: bspline ~1.57x1.36mm, area 1mm2, adj f13,f22,f48,f51
PART D: same geometry as A
PART E: same geometry as B
PLACE A rot(axis=(-1,0,0),90deg) t=(48.76,-3.89,-1.66)mm
PLACE B rot(axis=(0,-0.71,0.71),180deg) t=(75.03,1.51,-2.11)mm
PLACE C rot(axis=(-1,0,0),90deg) t=(100.59,-4.74,9.79)mm
PLACE D rot(axis=(-1,0,0),90deg) t=(-1.13,-4.08,-1.66)mm fixed
PLACE E rot(axis=(0,-0.71,0.71),180deg) t=(20.95,1,-2.11)mm
MATE planar C.f27 <-> B.f143  axis (0,0,-1) through (100.59,9.64,0.27)mm
MATE planar E.f143 <-> D.f23  axis (0,0,-1) through (20.95,-11.44,0.27)mm
MATE planar E.f143 <-> B.f143  axis (0,0,-1) through (20.95,-11.44,0.27)mm
MATE planar E.f143 <-> A.f23  axis (0,0,-1) through (20.95,-11.44,0.27)mm
